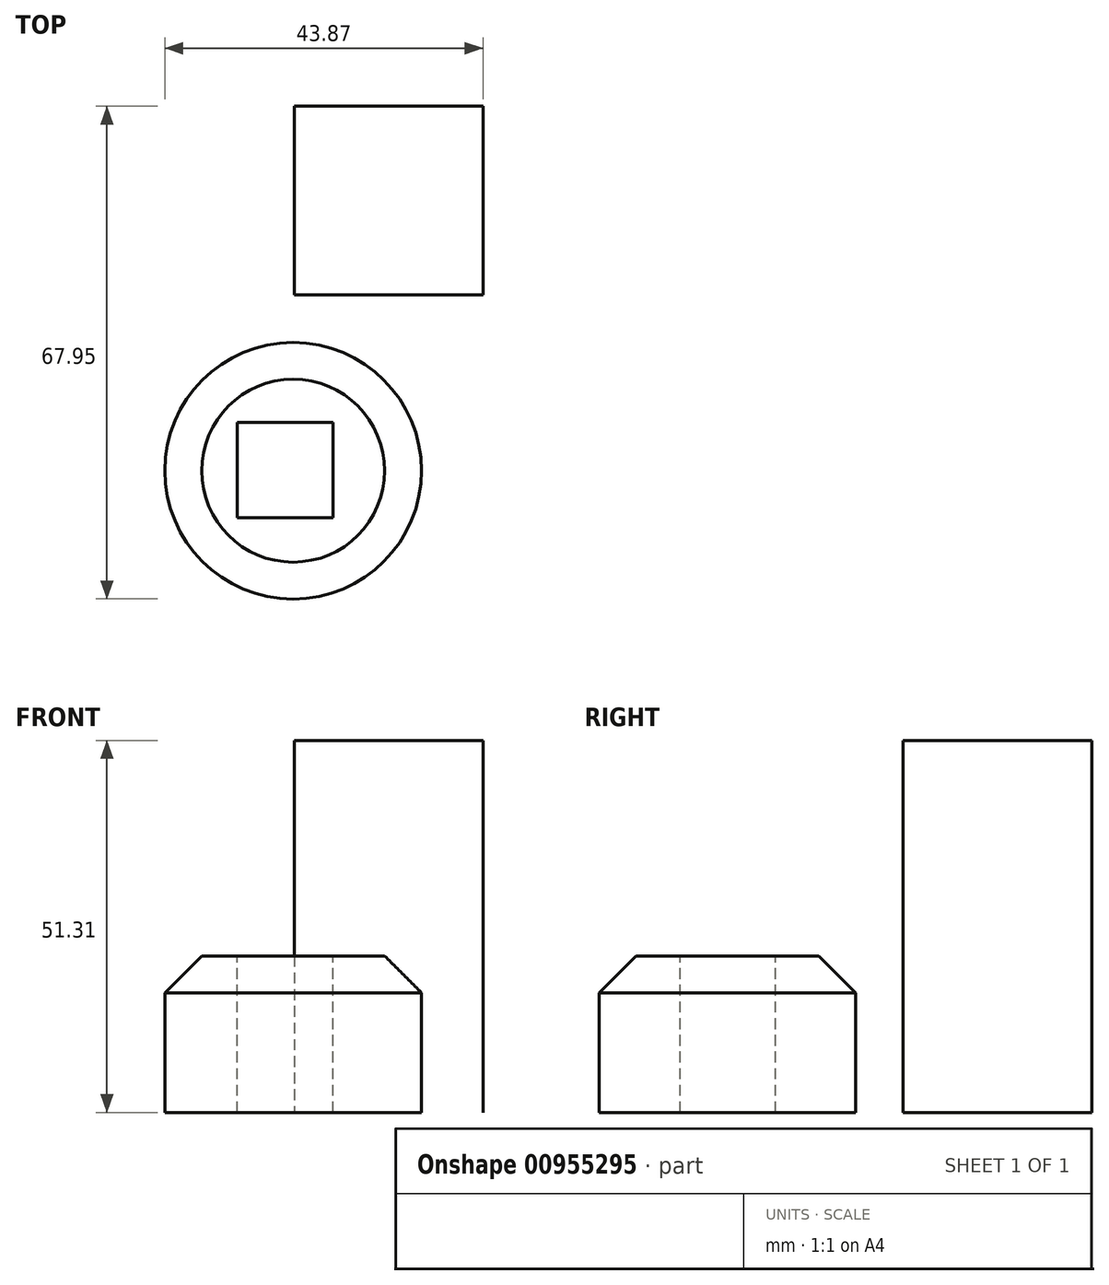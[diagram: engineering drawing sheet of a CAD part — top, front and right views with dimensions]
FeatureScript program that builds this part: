
annotation { "Feature Type Name" : "Feature", "Feature Type Description" : "" }
export const myFeature = defineFeature(function(context is Context, id is Id, definition is map)
    precondition{}
    {
        {
            var Q0;
            Q0=qCreatedBy(makeId("Top.planeOp"),FACE);
            var sketch = newSketch(context, id + "F0", { "sketchPlane" : qUnion([Q0])});
            skLineSegment(sketch, "E0.bottom", {"start": v(-122.93, 47.78) * mm, "end": v(-96.94, 47.78) * mm});
            skLineSegment(sketch, "E0.top", {"start": v(-122.93, 21.8) * mm, "end": v(-96.94, 21.8) * mm});
            skLineSegment(sketch, "E0.left", {"start": v(-122.93, 47.78) * mm, "end": v(-122.93, 21.8) * mm});
            skLineSegment(sketch, "E0.right", {"start": v(-96.94, 47.78) * mm, "end": v(-96.94, 21.8) * mm});
            skSolve(sketch);
        }
        {
            var Q0;
            Q0=makeQuery(id+"F0.imprint","IMPRINT",FACE,{"disambiguationData":[TD([[makeQuery(id+"F0.imprint","IMPRINT",EDGE,{"derivedFrom":sQuery(id+"F0.wireOp",EDGE,"E0.bottom")}),-1.0]])]});
            extrude(context, id + "F1", {"entities" : qUnion([Q0]), "depth" : 51.3 * mm, "offsetDistance" : 25.4 * mm});
        }
        {
            var Q0;
            Q0=qCreatedBy(makeId("Top.planeOp"),FACE);
            var sketch = newSketch(context, id + "F2", { "sketchPlane" : qUnion([Q0])});
            skCircle(sketch, "E1", {"center": v(-123.11, -2.48) * mm, "radius": 17.7 * mm});
            skSolve(sketch);
        }
        {
            var Q0;
            Q0=makeQuery(id+"F2.imprint","IMPRINT",FACE,{"disambiguationData":[TD([[makeQuery(id+"F2.imprint","IMPRINT",EDGE,{"derivedFrom":sQuery(id+"F2.wireOp",EDGE,"E1")}),1.0]])]});
            extrude(context, id + "F3", {"entities" : qUnion([Q0]), "depth" : 21.59 * mm, "offsetDistance" : 25.4 * mm});
        }
        {
            var Q0;
            Q0=makeQuery(id+"F3.opExtrude","CAP_FACE",FACE,{"disambiguationData":[OSD([sQuery(id+"F2.wireOp",EDGE,"E1")])],"isStart":false});
            var sketch = newSketch(context, id + "F4", { "sketchPlane" : qUnion([Q0])});
            skLineSegment(sketch, "E2.bottom", {"start": v(-130.8, 4.2) * mm, "end": v(-117.63, 4.2) * mm});
            skLineSegment(sketch, "E2.top", {"start": v(-130.8, -8.99) * mm, "end": v(-117.63, -8.99) * mm});
            skLineSegment(sketch, "E2.left", {"start": v(-130.8, 4.2) * mm, "end": v(-130.8, -8.99) * mm});
            skLineSegment(sketch, "E2.right", {"start": v(-117.63, 4.2) * mm, "end": v(-117.63, -8.99) * mm});
            skSolve(sketch);
        }
        {
            var Q0;
            Q0=makeQuery(id+"F4.imprint","IMPRINT",FACE,{"disambiguationData":[TD([[makeQuery(id+"F4.imprint","IMPRINT",EDGE,{"derivedFrom":sQuery(id+"F4.wireOp",EDGE,"E2.bottom")}),-1.0]])]});
            extrude(context, id + "F5", {"entities" : qUnion([Q0]), "operationType" : NewBodyOperationType.REMOVE, "oppositeDirection" : true, "depth" : 25.4 * mm, "offsetDistance" : 25.4 * mm});
        }
        {
            var Q0;
            Q0=makeQuery(id+"F3.opExtrude","CAP_FACE",FACE,{"disambiguationData":[OSD([sQuery(id+"F2.wireOp",EDGE,"E1")])],"isStart":false});
            extrude(context, id + "F6", {"entities" : qUnion([Q0]), "operationType" : NewBodyOperationType.REMOVE, "depth" : 65.28 * mm, "offsetDistance" : 25.4 * mm});
        }
        {
            var Q0;
            Q0=makeQuery(id+"F3.opExtrude","CAP_EDGE",EDGE,{"disambiguationData":[OSD([sQuery(id+"F2.wireOp",EDGE,"E1")])],"isStart":false});
            chamfer(context, id + "F7", {"entities" : qUnion([Q0]), "width" : 5.08 * mm, "tangentPropagation" : true});
        }
    });
